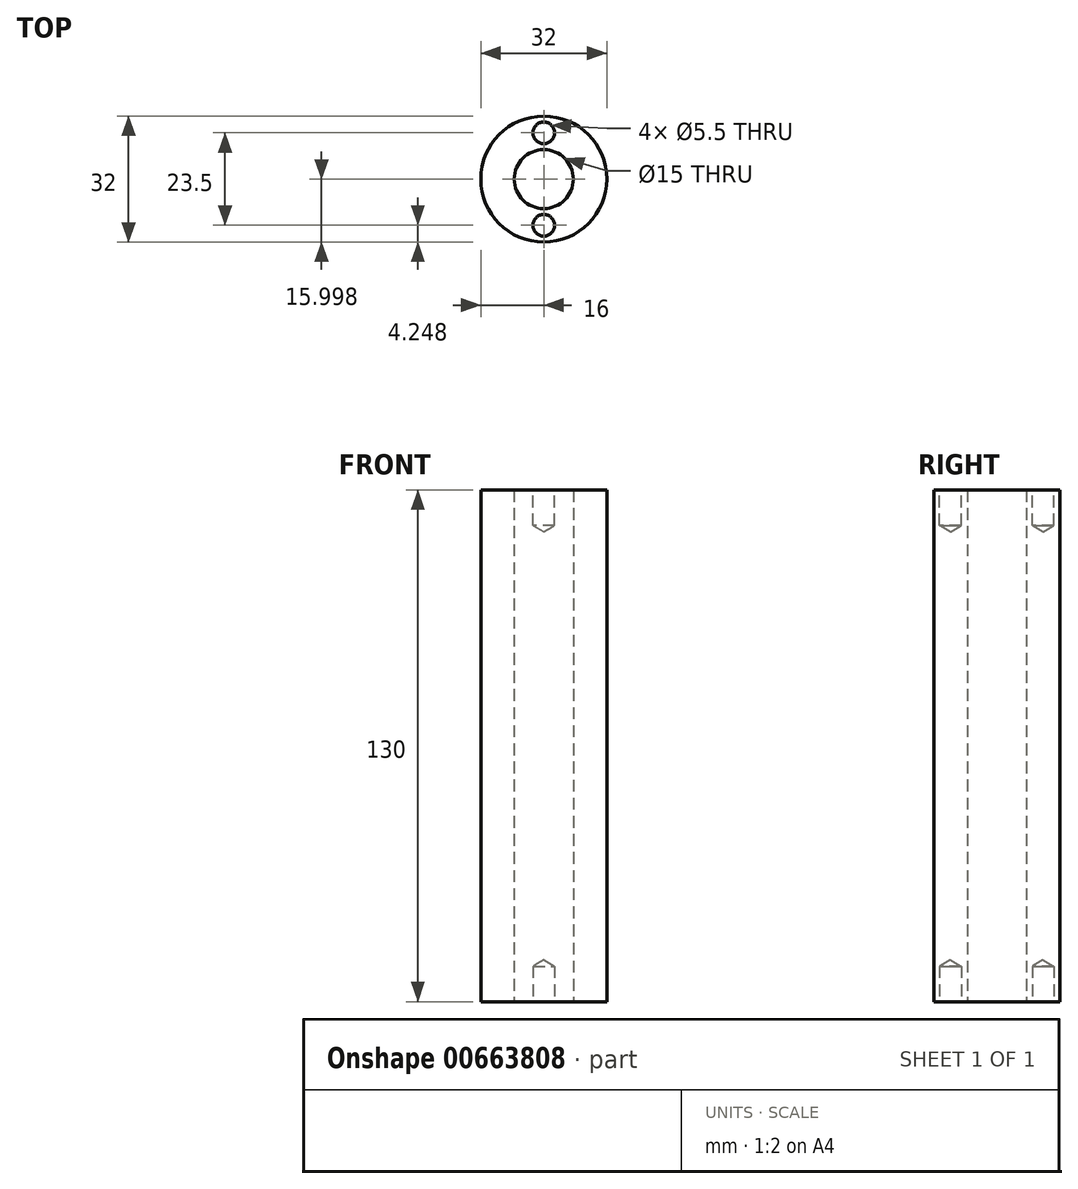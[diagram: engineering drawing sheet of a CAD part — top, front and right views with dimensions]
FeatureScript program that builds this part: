
annotation { "Feature Type Name" : "Feature", "Feature Type Description" : "" }
export const myFeature = defineFeature(function(context is Context, id is Id, definition is map)
    precondition{}
    {
        {
            var Q0;
            Q0=qCreatedBy(makeId("Top.planeOp"),FACE);
            var sketch = newSketch(context, id + "F0", { "sketchPlane" : qUnion([Q0])});
            skCircle(sketch, "E0", {"center": v(0, -0.45) * mm, "radius": 7.5 * mm});
            skCircle(sketch, "E1", {"center": v(0, -0.45) * mm, "radius": 16 * mm});
            skSolve(sketch);
        }
        {
            var Q0;
            Q0 = qSketchRegion(id + "F0", true);
            extrude(context, id + "F1", {"entities" : qUnion([Q0]), "depth" : 130 * mm, "offsetDistance" : 25 * mm});
        }
        {
            var Q0;
            Q0=makeQuery(id+"F1.opExtrude","CAP_FACE",FACE,{"disambiguationData":[OSD([sQuery(id+"F0.wireOp",EDGE,"E0"),sQuery(id+"F0.wireOp",EDGE,"E1")])],"isStart":false});
            var sketch = newSketch(context, id + "F2", { "sketchPlane" : qUnion([Q0])});
            skPoint(sketch, "E2", {"position": v(0, 11.3) * mm});
            skPoint(sketch, "E3", {"position": v(0, -12.2) * mm});
            skSolve(sketch);
        }
        {
            var Q0;
            Q0=sQuery(id+"F2.wireOp",VERTEX,"E2");
            var Q1;
            Q1=makeQuery(id+"F1.opExtrude","SWEPT_BODY",BODY,{"disambiguationData":[OSD([sQuery(id+"F0.wireOp",EDGE,"E0"),sQuery(id+"F0.wireOp",EDGE,"E1")])]});
            hole(context, id + "F3", {"style" : HoleStyle.SIMPLE, "endStyle" : HoleEndStyle.BLIND, "holeDiameter" : 5.5 * mm, "majorDiameter" : 5 * mm, "holeDepth" : 9 * mm, "isTappedThrough" : true, "tappedDepth" : 12 * mm, "tapClearance" : 3, "locations" : qUnion([Q0]), "scope" : qUnion([Q1])});
        }
        {
            var Q0;
            Q0=sQuery(id+"F2.wireOp",VERTEX,"E3");
            var Q1;
            Q1=makeQuery(id+"F1.opExtrude","SWEPT_BODY",BODY,{"disambiguationData":[OSD([sQuery(id+"F0.wireOp",EDGE,"E0"),sQuery(id+"F0.wireOp",EDGE,"E1")])]});
            hole(context, id + "F4", {"style" : HoleStyle.SIMPLE, "endStyle" : HoleEndStyle.BLIND, "holeDiameter" : 5.5 * mm, "majorDiameter" : 5 * mm, "holeDepth" : 9 * mm, "isTappedThrough" : true, "tappedDepth" : 12 * mm, "tapClearance" : 3, "locations" : qUnion([Q0]), "scope" : qUnion([Q1])});
        }
        {
            var Q0;
            Q0=qCreatedBy(makeId("Top.planeOp"),FACE);
            var sketch = newSketch(context, id + "F5", { "sketchPlane" : qUnion([Q0])});
            skPoint(sketch, "E4", {"position": v(0, -12.2) * mm});
            skPoint(sketch, "E5", {"position": v(0, 11.3) * mm});
            skSolve(sketch);
        }
        {
            var Q0;
            Q0=sQuery(id+"F5.wireOp",VERTEX,"E5");
            var Q1;
            Q1=makeQuery(id+"F1.opExtrude","SWEPT_BODY",BODY,{"disambiguationData":[OSD([sQuery(id+"F0.wireOp",EDGE,"E0"),sQuery(id+"F0.wireOp",EDGE,"E1")])]});
            hole(context, id + "F6", {"style" : HoleStyle.SIMPLE, "endStyle" : HoleEndStyle.BLIND, "oppositeDirection" : true, "holeDiameter" : 5.5 * mm, "majorDiameter" : 5 * mm, "holeDepth" : 9 * mm, "isTappedThrough" : true, "tappedDepth" : 12 * mm, "tapClearance" : 3, "locations" : qUnion([Q0]), "scope" : qUnion([Q1])});
        }
        {
            var Q0;
            Q0=sQuery(id+"F5.wireOp",VERTEX,"E4");
            var Q1;
            Q1=makeQuery(id+"F1.opExtrude","SWEPT_BODY",BODY,{"disambiguationData":[OSD([sQuery(id+"F0.wireOp",EDGE,"E0"),sQuery(id+"F0.wireOp",EDGE,"E1")])]});
            hole(context, id + "F7", {"style" : HoleStyle.SIMPLE, "endStyle" : HoleEndStyle.BLIND, "oppositeDirection" : true, "holeDiameter" : 5.5 * mm, "majorDiameter" : 5 * mm, "holeDepth" : 9 * mm, "isTappedThrough" : true, "tappedDepth" : 12 * mm, "tapClearance" : 3, "locations" : qUnion([Q0]), "scope" : qUnion([Q1])});
        }
    });
